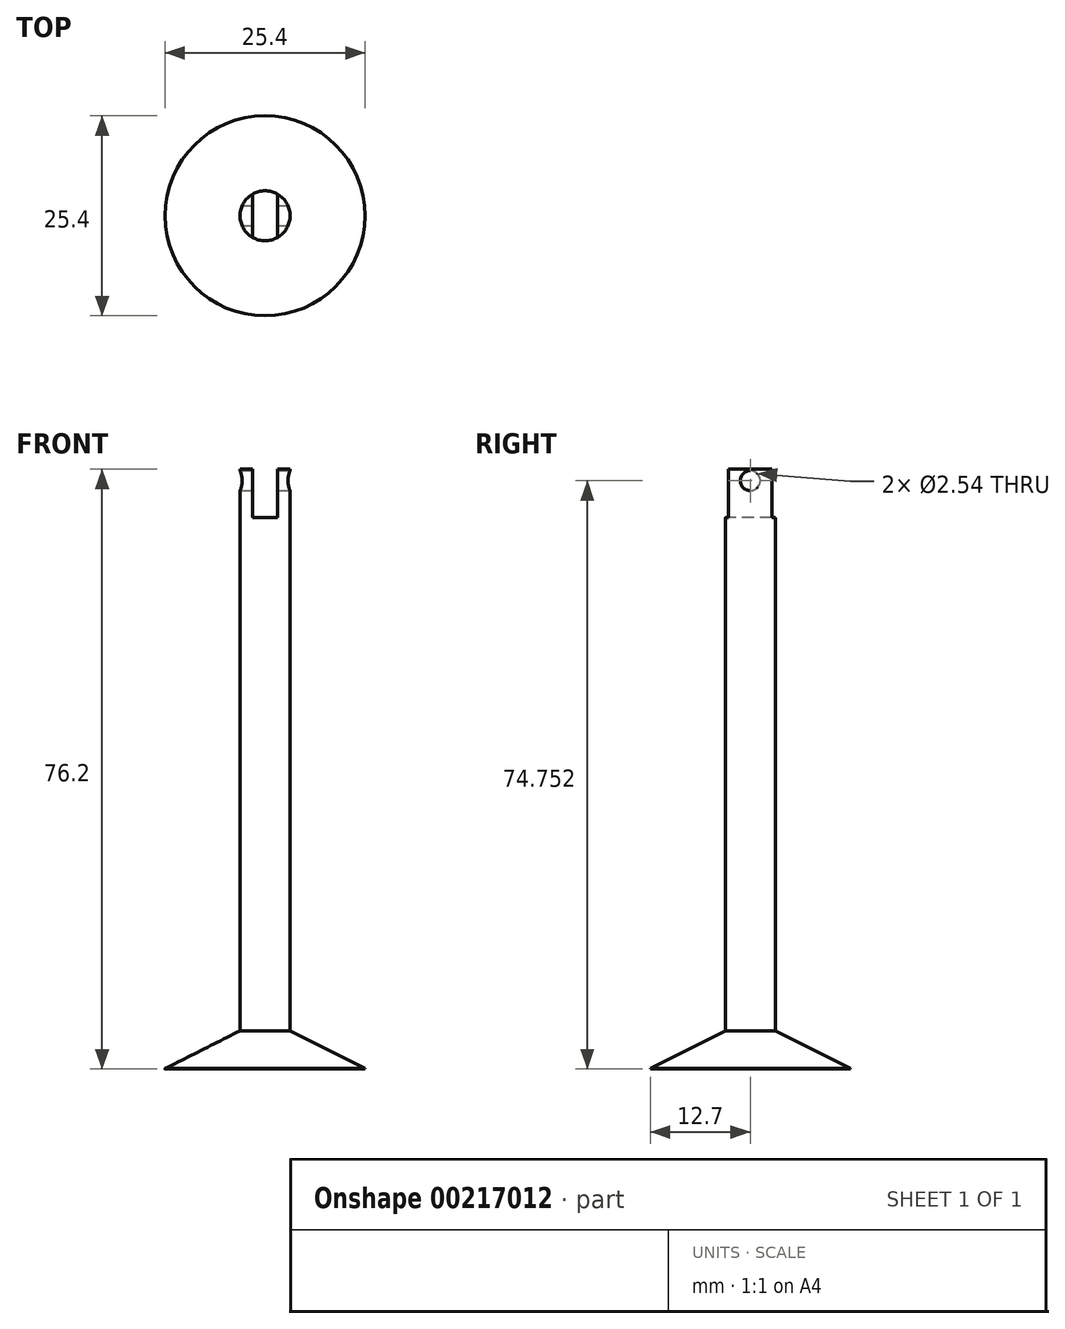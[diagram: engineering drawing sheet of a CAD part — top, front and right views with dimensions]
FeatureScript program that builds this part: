
annotation { "Feature Type Name" : "Feature", "Feature Type Description" : "" }
export const myFeature = defineFeature(function(context is Context, id is Id, definition is map)
    precondition{}
    {
        {
            var Q0;
            Q0=qCreatedBy(makeId("Top.planeOp"),FACE);
            var sketch = newSketch(context, id + "F0", { "sketchPlane" : qUnion([Q0])});
            skCircle(sketch, "E0", {"center": v(0, 0) * mm, "radius": 12.7 * mm});
            skSolve(sketch);
        }
        {
            var Q0;
            Q0 = qSketchRegion(id + "F0", true);
            extrude(context, id + "F1", {"entities" : qUnion([Q0]), "depth" : 76.2 * mm});
        }
        {
            var Q0;
            Q0=qCreatedBy(makeId("Front.planeOp"),FACE);
            var sketch = newSketch(context, id + "F2", { "sketchPlane" : qUnion([Q0])});
            skLineSegment(sketch, "E1.bottom", {"start": v(3.17, 0) * mm, "end": v(-3.18, 0) * mm});
            skLineSegment(sketch, "E1.top", {"start": v(3.17, 153.74) * mm, "end": v(-3.18, 153.74) * mm});
            skLineSegment(sketch, "E1.left", {"start": v(3.17, 0) * mm, "end": v(3.17, 153.74) * mm});
            skLineSegment(sketch, "E1.right", {"start": v(-3.18, 0) * mm, "end": v(-3.18, 153.74) * mm});
            skPoint(sketch, "E1.middle", {"position": v(0, 76.87) * mm});
            skLineSegment(sketch, "E2", {"start": v(-3.18, 4.87) * mm, "end": v(-17.21, -2.22) * mm});
            skLineSegment(sketch, "E3", {"start": v(-17.21, -2.22) * mm, "end": v(-17.21, 83.75) * mm});
            skLineSegment(sketch, "E4", {"start": v(-17.21, 83.75) * mm, "end": v(-3.18, 83.75) * mm});
            skSolve(sketch);
        }
        {
            var Q0;
            {var subQ0=sQuery(id+"F2.wireOp",EDGE,"E2");Q0=makeQuery(id+"F2.imprint","IMPRINT",FACE,{"disambiguationData":[TD([[makeQuery(id+"F2.imprint","IMPRINT",EDGE,{"derivedFrom":subQ0}),-1.0]])]});}
            var Q1;
            Q1=makeQuery(id+"F1.opExtrude","CAP_EDGE",EDGE,{"disambiguationData":[OSD([sQuery(id+"F0.wireOp",EDGE,"E0")])],"isStart":false});
            revolve(context, id + "F3", {"operationType" : NewBodyOperationType.REMOVE, "entities" : qUnion([Q0]), "axis" : qUnion([Q1]), "revolveType" : RevolveType.FULL, "oppositeDirection" : true});
        }
        {
            var Q0;
            Q0=qCreatedBy(makeId("Front.planeOp"),FACE);
            var sketch = newSketch(context, id + "F4", { "sketchPlane" : qUnion([Q0])});
            skLineSegment(sketch, "E5.bottom", {"start": v(1.59, 70.06) * mm, "end": v(-1.59, 70.06) * mm});
            skLineSegment(sketch, "E5.top", {"start": v(1.59, 82.76) * mm, "end": v(-1.59, 82.76) * mm});
            skLineSegment(sketch, "E5.left", {"start": v(1.59, 70.06) * mm, "end": v(1.59, 82.76) * mm});
            skLineSegment(sketch, "E5.right", {"start": v(-1.59, 70.06) * mm, "end": v(-1.59, 82.76) * mm});
            skPoint(sketch, "E5.middle", {"position": v(0, 76.4) * mm});
            skSolve(sketch);
        }
        {
            var Q0;
            Q0=makeQuery(id+"F4.imprint","IMPRINT",FACE,{"disambiguationData":[TD([[makeQuery(id+"F4.imprint","IMPRINT",EDGE,{"derivedFrom":sQuery(id+"F4.wireOp",EDGE,"E5.bottom")}),-1.0]])]});
            extrude(context, id + "F5", {"entities" : qUnion([Q0]), "operationType" : NewBodyOperationType.REMOVE, "oppositeDirection" : true, "depth" : 25.4 * mm, "symmetric" : true});
        }
        {
            var Q0;
            Q0=qCreatedBy(makeId("Right.planeOp"),FACE);
            var sketch = newSketch(context, id + "F6", { "sketchPlane" : qUnion([Q0])});
            skCircle(sketch, "E6", {"center": v(0, 74.75) * mm, "radius": 4.45 * mm});
            skCircle(sketch, "E7", {"center": v(0, 74.75) * mm, "radius": 1.27 * mm});
            skSolve(sketch);
        }
        {
            var Q0;
            Q0=makeQuery(id+"F6.imprint","IMPRINT",FACE,{"disambiguationData":[TD([[makeQuery(id+"F6.imprint","IMPRINT",EDGE,{"derivedFrom":sQuery(id+"F6.wireOp",EDGE,"E7")}),1.0]])]});
            extrude(context, id + "F7", {"entities" : qUnion([Q0]), "operationType" : NewBodyOperationType.REMOVE, "oppositeDirection" : true, "depth" : 25.4 * mm, "symmetric" : true});
        }
    });
